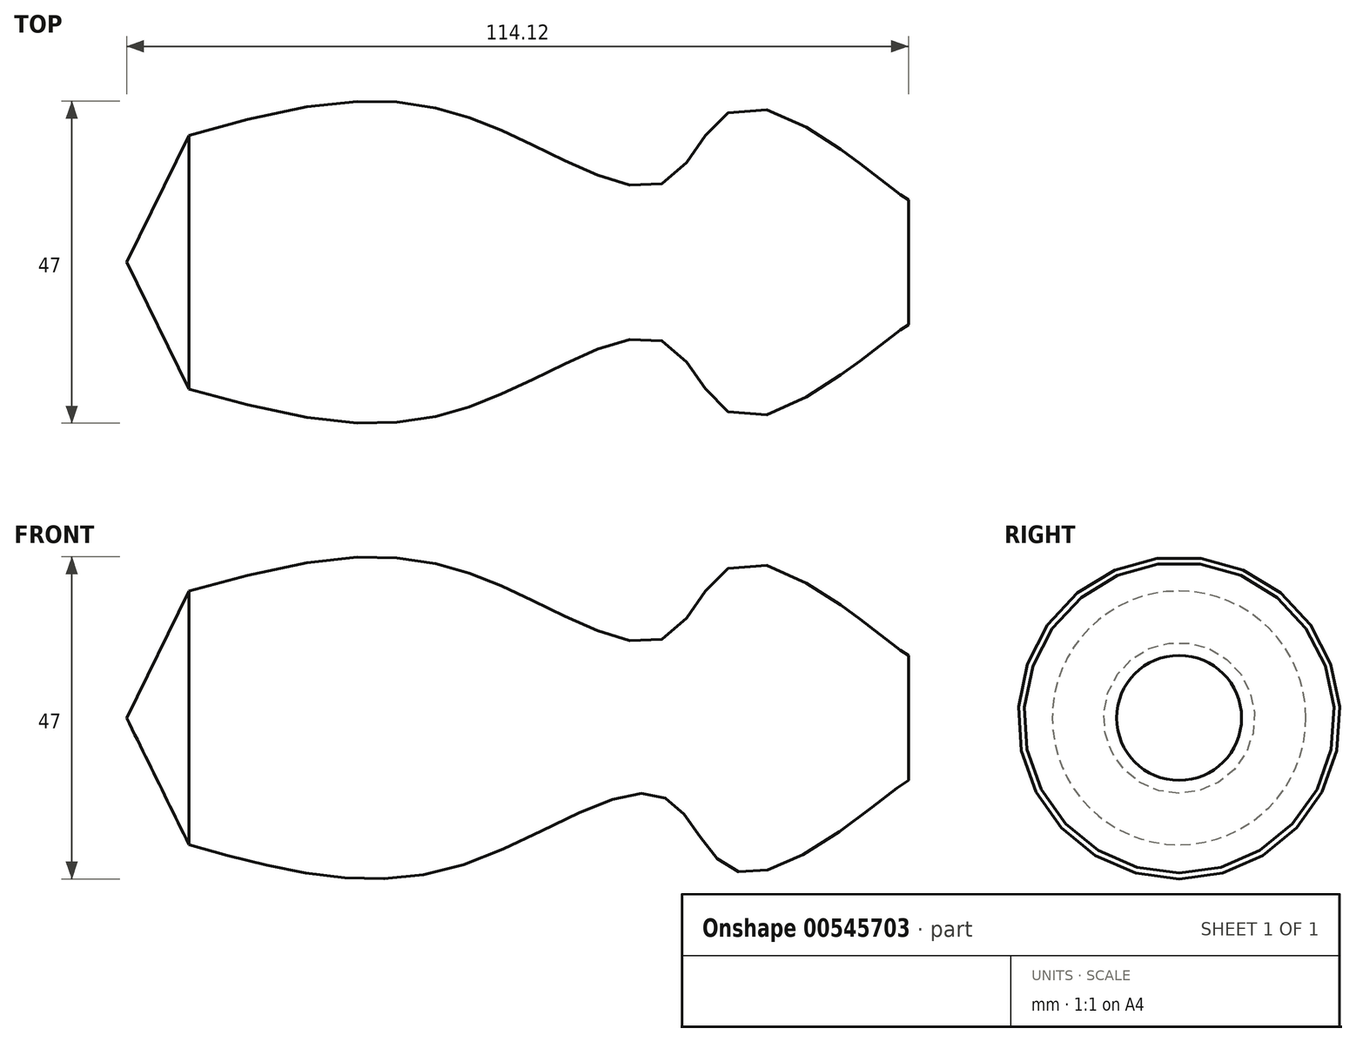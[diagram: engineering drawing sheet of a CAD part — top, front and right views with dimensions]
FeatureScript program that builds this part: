
annotation { "Feature Type Name" : "Feature", "Feature Type Description" : "" }
export const myFeature = defineFeature(function(context is Context, id is Id, definition is map)
    precondition{}
    {
        {
            var Q0;
            Q0=qCreatedBy(makeId("Front.planeOp"),FACE);
            var sketch = newSketch(context, id + "F0", { "sketchPlane" : qUnion([Q0])});
            skFitSpline(sketch, "E0", {"points": [v(-45.87, 18.51) * mm, v(-7.18, 21.83) * mm, v(23.49, 11.6) * mm, v(35.64, 22.66) * mm, v(59.13, 9.12) * mm, v(59.13, 9.4) * mm], "startDerivative": vector(133.52, 37.55) * mm, "endDerivative": vector(-5.87, 17.2) * mm});
            skLineSegment(sketch, "E1", {"start": v(-45.87, 18.51) * mm, "end": v(-54.99, 0) * mm});
            skLineSegment(sketch, "E2", {"start": v(59.13, 9.12) * mm, "end": v(59.13, 0) * mm});
            skLineSegment(sketch, "E3", {"start": v(59.13, 0) * mm, "end": v(-54.99, 0) * mm});
            skSolve(sketch);
        }
        {
            var Q0;
            {var subQ0=sQuery(id+"F0.wireOp",EDGE,"E1");Q0=makeQuery(id+"F0.imprint","IMPRINT",FACE,{"disambiguationData":[TD([[makeQuery(id+"F0.imprint","IMPRINT",EDGE,{"derivedFrom":subQ0}),1.0]])]});}
            var Q1;
            Q1=sQuery(id+"F0.wireOp",EDGE,"E3");
            revolve(context, id + "F1", {"entities" : qUnion([Q0]), "axis" : qUnion([Q1]), "revolveType" : RevolveType.FULL});
        }
    });
